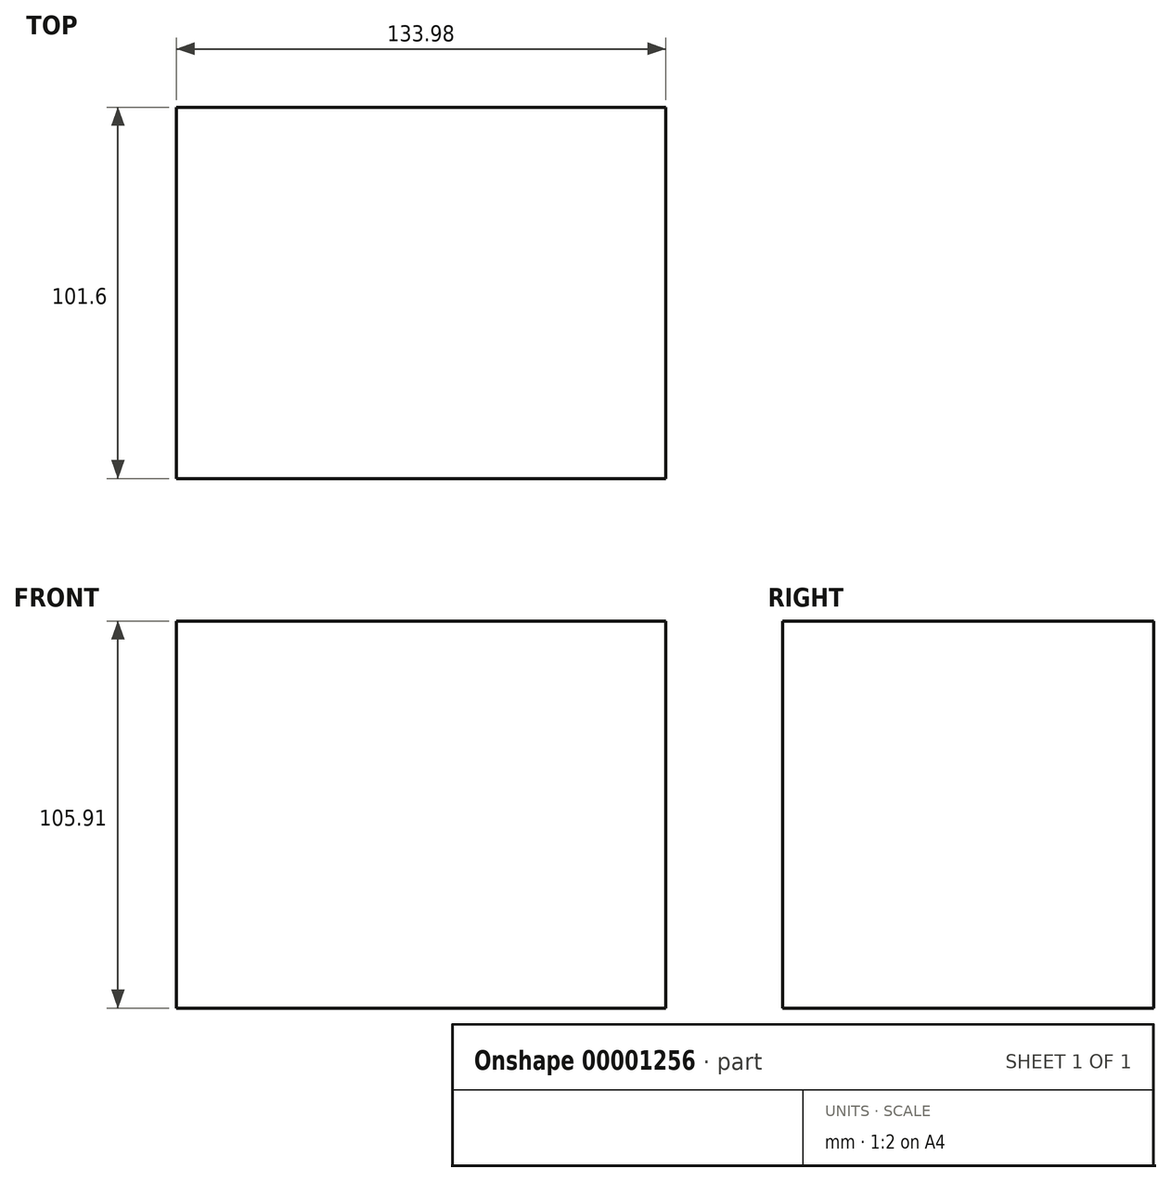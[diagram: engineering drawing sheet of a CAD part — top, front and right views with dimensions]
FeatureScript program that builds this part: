
annotation { "Feature Type Name" : "Feature", "Feature Type Description" : "" }
export const myFeature = defineFeature(function(context is Context, id is Id, definition is map)
    precondition{}
    {
        {
            var Q0;
            Q0=qCreatedBy(makeId("Front.planeOp"),FACE);
            var sketch = newSketch(context, id + "F0", { "sketchPlane" : qUnion([Q0])});
            skLineSegment(sketch, "E0.bottom", {"start": v(-68.02, 58.92) * mm, "end": v(65.96, 58.92) * mm});
            skLineSegment(sketch, "E0.top", {"start": v(-68.02, -46.99) * mm, "end": v(65.96, -46.99) * mm});
            skLineSegment(sketch, "E0.left", {"start": v(-68.02, 58.92) * mm, "end": v(-68.02, -46.99) * mm});
            skLineSegment(sketch, "E0.right", {"start": v(65.96, 58.92) * mm, "end": v(65.96, -46.99) * mm});
            skSolve(sketch);
        }
        {
            var Q0;
            Q0 = qSketchRegion(id + "F0", true);
            extrude(context, id + "F1", {"entities" : qUnion([Q0]), "depth" : 101.6 * mm});
        }
    });
